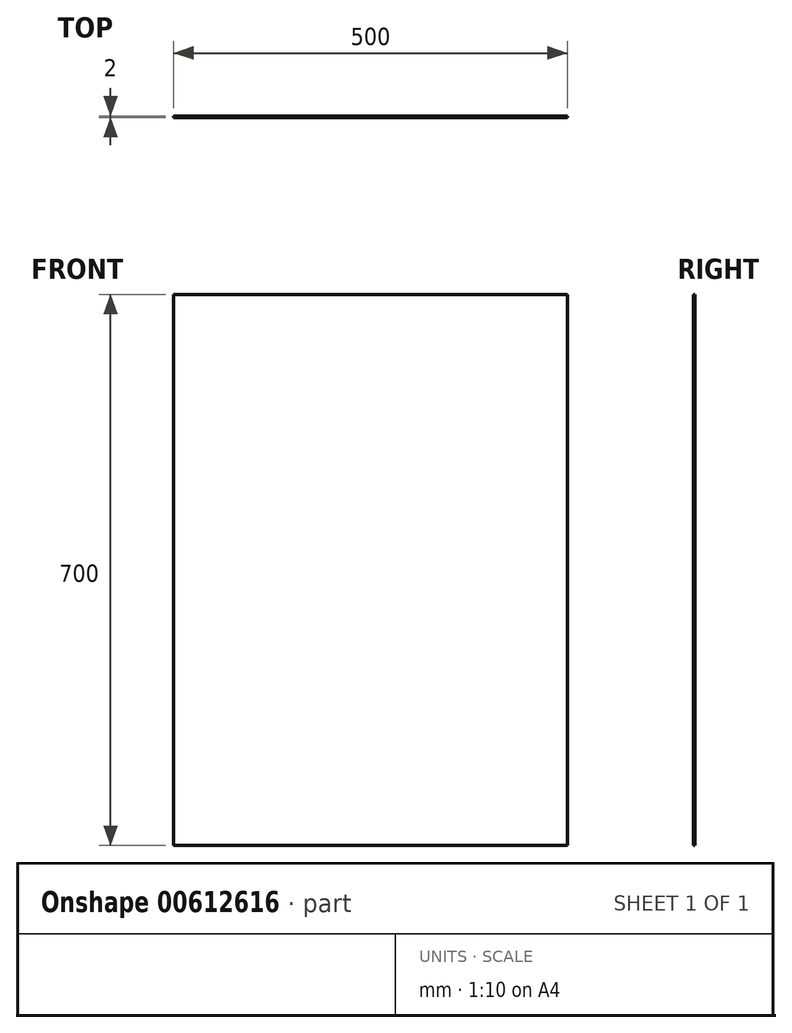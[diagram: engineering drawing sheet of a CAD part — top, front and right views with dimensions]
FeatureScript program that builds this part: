
annotation { "Feature Type Name" : "Feature", "Feature Type Description" : "" }
export const myFeature = defineFeature(function(context is Context, id is Id, definition is map)
    precondition{}
    {
        {
            var Q0;
            Q0=qCreatedBy(makeId("Front.planeOp"),FACE);
            var sketch = newSketch(context, id + "F0", { "sketchPlane" : qUnion([Q0])});
            skLineSegment(sketch, "E0.bottom", {"start": v(-250, 350) * mm, "end": v(250, 350) * mm});
            skLineSegment(sketch, "E0.top", {"start": v(-250, -350) * mm, "end": v(250, -350) * mm});
            skLineSegment(sketch, "E0.left", {"start": v(-250, 350) * mm, "end": v(-250, -350) * mm});
            skLineSegment(sketch, "E0.right", {"start": v(250, 350) * mm, "end": v(250, -350) * mm});
            skPoint(sketch, "E0.middle", {"position": v(0, 0) * mm});
            skSolve(sketch);
        }
        {
            var Q0;
            Q0=makeQuery(id+"F0.imprint","IMPRINT",FACE,{"disambiguationData":[TD([[makeQuery(id+"F0.imprint","IMPRINT",EDGE,{"derivedFrom":sQuery(id+"F0.wireOp",EDGE,"E0.bottom")}),-1.0]])]});
            extrude(context, id + "F1", {"entities" : qUnion([Q0]), "depth" : 2 * mm, "offsetDistance" : 25.4 * mm});
        }
    });
